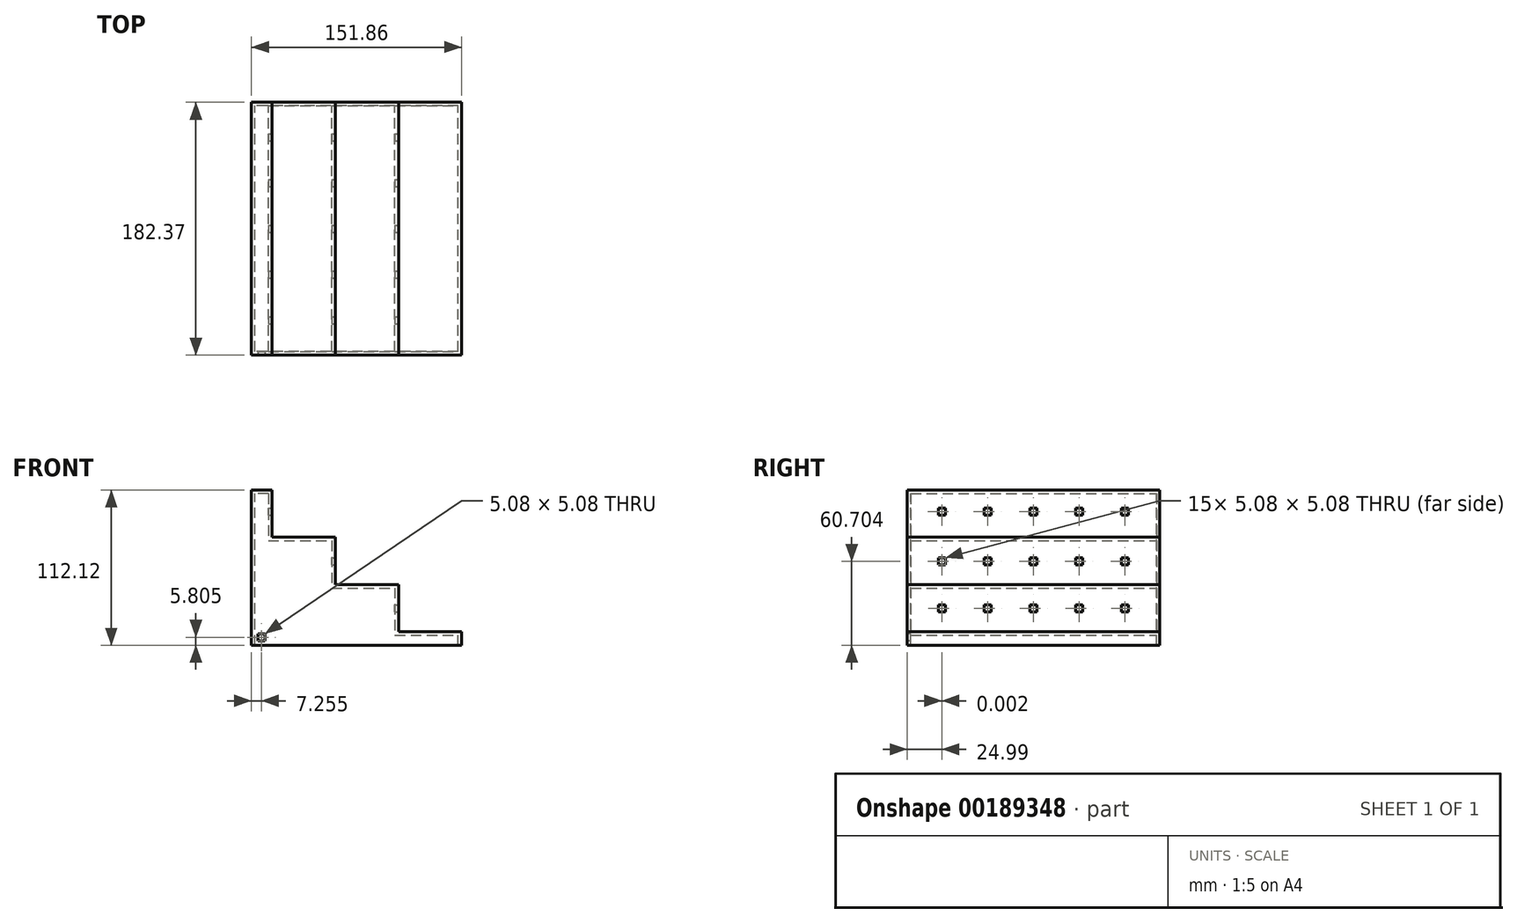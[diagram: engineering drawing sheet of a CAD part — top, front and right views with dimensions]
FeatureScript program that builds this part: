
annotation { "Feature Type Name" : "Feature", "Feature Type Description" : "" }
export const myFeature = defineFeature(function(context is Context, id is Id, definition is map)
    precondition{}
    {
        {
            var Q0;
            Q0=qCreatedBy(makeId("Front.planeOp"),FACE);
            var sketch = newSketch(context, id + "F0", { "sketchPlane" : qUnion([Q0])});
            skLineSegment(sketch, "E0.bottom", {"start": v(75.93, -56.06) * mm, "end": v(-75.93, -56.06) * mm});
            skLineSegment(sketch, "E0.top", {"start": v(75.93, 56.06) * mm, "end": v(-75.93, 56.06) * mm});
            skLineSegment(sketch, "E0.left", {"start": v(75.93, -56.06) * mm, "end": v(75.93, 56.06) * mm});
            skLineSegment(sketch, "E0.right", {"start": v(-75.93, -56.06) * mm, "end": v(-75.93, 56.06) * mm});
            skPoint(sketch, "E0.middle", {"position": v(0, 0) * mm});
            skLineSegment(sketch, "E1", {"start": v(-61.23, 56.06) * mm, "end": v(-61.23, -56.06) * mm});
            skLineSegment(sketch, "E2", {"start": v(-15.51, 56.06) * mm, "end": v(-15.51, -56.06) * mm});
            skLineSegment(sketch, "E3", {"start": v(30.2, 56.06) * mm, "end": v(30.2, -56.06) * mm});
            skLineSegment(sketch, "E4", {"start": v(-75.93, -46.26) * mm, "end": v(75.93, -46.26) * mm});
            skLineSegment(sketch, "E5", {"start": v(-75.93, 21.96) * mm, "end": v(75.93, 21.96) * mm});
            skLineSegment(sketch, "E6", {"start": v(-75.93, -12.15) * mm, "end": v(75.93, -12.15) * mm});
            skSolve(sketch);
        }
        {
            var Q0;
            {var subQ0=sQuery(id+"F0.wireOp",EDGE,"E0.right");var subQ1=sQuery(id+"F0.wireOp",EDGE,"E0.top");var subQ2=makeQuery(id+"F0.imprint","INTERSECT",VERTEX,{"derivedFrom":[subQ1,subQ0]});Q0=makeQuery(id+"F0.imprint","IMPRINT",FACE,{"disambiguationData":[TD([[makeQuery(id+"F0.imprint","IMPRINT",EDGE,{"disambiguationData":[TD([[subQ2,1.0]])],"derivedFrom":subQ1}),1.0]])]});}
            var Q1;
            {var subQ0=sQuery(id+"F0.wireOp",EDGE,"E5");var subQ1=sQuery(id+"F0.wireOp",EDGE,"E1");var subQ2=makeQuery(id+"F0.imprint","INTERSECT",VERTEX,{"derivedFrom":[subQ1,subQ0]});Q1=makeQuery(id+"F0.imprint","IMPRINT",FACE,{"disambiguationData":[TD([[makeQuery(id+"F0.imprint","IMPRINT",EDGE,{"disambiguationData":[TD([[subQ2,-1.0]])],"derivedFrom":subQ1}),1.0]])]});}
            var Q2;
            {var subQ0=sQuery(id+"F0.wireOp",EDGE,"E5");var subQ1=sQuery(id+"F0.wireOp",EDGE,"E0.right");var subQ2=makeQuery(id+"F0.imprint","INTERSECT",VERTEX,{"derivedFrom":[subQ1,subQ0]});Q2=makeQuery(id+"F0.imprint","IMPRINT",FACE,{"disambiguationData":[TD([[makeQuery(id+"F0.imprint","IMPRINT",EDGE,{"disambiguationData":[TD([[subQ2,1.0]])],"derivedFrom":subQ1}),-1.0]])]});}
            var Q3;
            {var subQ0=sQuery(id+"F0.wireOp",EDGE,"E4");var subQ1=sQuery(id+"F0.wireOp",EDGE,"E0.right");var subQ2=makeQuery(id+"F0.imprint","INTERSECT",VERTEX,{"derivedFrom":[subQ1,subQ0]});Q3=makeQuery(id+"F0.imprint","IMPRINT",FACE,{"disambiguationData":[TD([[makeQuery(id+"F0.imprint","IMPRINT",EDGE,{"disambiguationData":[TD([[subQ2,-1.0]])],"derivedFrom":subQ1}),-1.0]])]});}
            var Q4;
            {var subQ0=sQuery(id+"F0.wireOp",EDGE,"E0.right");var subQ1=sQuery(id+"F0.wireOp",EDGE,"E0.bottom");var subQ2=makeQuery(id+"F0.imprint","INTERSECT",VERTEX,{"derivedFrom":[subQ1,subQ0]});Q4=makeQuery(id+"F0.imprint","IMPRINT",FACE,{"disambiguationData":[TD([[makeQuery(id+"F0.imprint","IMPRINT",EDGE,{"disambiguationData":[TD([[subQ2,1.0]])],"derivedFrom":subQ1}),-1.0]])]});}
            var Q5;
            {var subQ0=sQuery(id+"F0.wireOp",EDGE,"E6");var subQ1=sQuery(id+"F0.wireOp",EDGE,"E1");var subQ2=makeQuery(id+"F0.imprint","INTERSECT",VERTEX,{"derivedFrom":[subQ1,subQ0]});Q5=makeQuery(id+"F0.imprint","IMPRINT",FACE,{"disambiguationData":[TD([[makeQuery(id+"F0.imprint","IMPRINT",EDGE,{"disambiguationData":[TD([[subQ2,-1.0]])],"derivedFrom":subQ1}),1.0]])]});}
            var Q6;
            {var subQ0=sQuery(id+"F0.wireOp",EDGE,"E1");var subQ1=sQuery(id+"F0.wireOp",EDGE,"E0.bottom");var subQ2=makeQuery(id+"F0.imprint","INTERSECT",VERTEX,{"derivedFrom":[subQ1,subQ0]});Q6=makeQuery(id+"F0.imprint","IMPRINT",FACE,{"disambiguationData":[TD([[makeQuery(id+"F0.imprint","IMPRINT",EDGE,{"disambiguationData":[TD([[subQ2,1.0]])],"derivedFrom":subQ1}),-1.0]])]});}
            var Q7;
            {var subQ0=sQuery(id+"F0.wireOp",EDGE,"E2");var subQ1=sQuery(id+"F0.wireOp",EDGE,"E0.bottom");var subQ2=makeQuery(id+"F0.imprint","INTERSECT",VERTEX,{"derivedFrom":[subQ1,subQ0]});Q7=makeQuery(id+"F0.imprint","IMPRINT",FACE,{"disambiguationData":[TD([[makeQuery(id+"F0.imprint","IMPRINT",EDGE,{"disambiguationData":[TD([[subQ2,1.0]])],"derivedFrom":subQ1}),-1.0]])]});}
            var Q8;
            {var subQ0=sQuery(id+"F0.wireOp",EDGE,"E0.left");var subQ1=sQuery(id+"F0.wireOp",EDGE,"E0.bottom");var subQ2=makeQuery(id+"F0.imprint","INTERSECT",VERTEX,{"derivedFrom":[subQ1,subQ0]});Q8=makeQuery(id+"F0.imprint","IMPRINT",FACE,{"disambiguationData":[TD([[makeQuery(id+"F0.imprint","IMPRINT",EDGE,{"disambiguationData":[TD([[subQ2,-1.0]])],"derivedFrom":subQ1}),-1.0]])]});}
            var Q9;
            {var subQ0=sQuery(id+"F0.wireOp",EDGE,"E6");var subQ1=sQuery(id+"F0.wireOp",EDGE,"E2");var subQ2=makeQuery(id+"F0.imprint","INTERSECT",VERTEX,{"derivedFrom":[subQ1,subQ0]});Q9=makeQuery(id+"F0.imprint","IMPRINT",FACE,{"disambiguationData":[TD([[makeQuery(id+"F0.imprint","IMPRINT",EDGE,{"disambiguationData":[TD([[subQ2,-1.0]])],"derivedFrom":subQ1}),1.0]])]});}
            extrude(context, id + "F1", {"entities" : qUnion([Q0, Q1, Q2, Q3, Q4, Q5, Q6, Q7, Q8, Q9]), "depth" : 182.37 * mm});
        }
        {
            var Q0;
            Q0=makeQuery(id+"F1.opExtrude","SWEPT_FACE",FACE,{"disambiguationData":[OSD([sQuery(id+"F0.wireOp",EDGE,"E0.bottom")])]});
            shell(context, id + "F2", {"entities" : qUnion([Q0]), "thickness" : 2.54 * mm});
        }
        {
            var Q0;
            Q0=makeQuery(id+"F1.opExtrude","SWEPT_FACE",FACE,{"disambiguationData":[OSD([sQuery(id+"F0.wireOp",EDGE,"E3")])]});
            var sketch = newSketch(context, id + "F3", { "sketchPlane" : qUnion([Q0])});
            skLineSegment(sketch, "E7", {"start": v(-182.37, -29.2) * mm, "end": v(0, -29.2) * mm});
            skLineSegment(sketch, "E8.bottom", {"start": v(-154.69, -31.75) * mm, "end": v(-159.77, -31.75) * mm});
            skLineSegment(sketch, "E8.top", {"start": v(-154.69, -26.67) * mm, "end": v(-159.77, -26.67) * mm});
            skLineSegment(sketch, "E8.left", {"start": v(-154.69, -31.75) * mm, "end": v(-154.69, -26.67) * mm});
            skLineSegment(sketch, "E8.right", {"start": v(-159.77, -31.75) * mm, "end": v(-159.77, -26.67) * mm});
            skPoint(sketch, "E8.middle", {"position": v(-157.23, -29.2) * mm});
            skLineSegment(sketch, "E9.bottom", {"start": v(-121.67, -31.75) * mm, "end": v(-126.75, -31.75) * mm});
            skLineSegment(sketch, "E9.top", {"start": v(-121.67, -26.67) * mm, "end": v(-126.75, -26.67) * mm});
            skLineSegment(sketch, "E9.left", {"start": v(-121.67, -31.75) * mm, "end": v(-121.67, -26.67) * mm});
            skLineSegment(sketch, "E9.right", {"start": v(-126.75, -31.75) * mm, "end": v(-126.75, -26.67) * mm});
            skPoint(sketch, "E9.middle", {"position": v(-124.2, -29.2) * mm});
            skLineSegment(sketch, "E10.bottom", {"start": v(-88.65, -31.75) * mm, "end": v(-93.73, -31.75) * mm});
            skLineSegment(sketch, "E10.top", {"start": v(-88.65, -26.67) * mm, "end": v(-93.73, -26.67) * mm});
            skLineSegment(sketch, "E10.left", {"start": v(-88.65, -31.75) * mm, "end": v(-88.65, -26.67) * mm});
            skLineSegment(sketch, "E10.right", {"start": v(-93.73, -31.75) * mm, "end": v(-93.73, -26.67) * mm});
            skPoint(sketch, "E10.middle", {"position": v(-91.19, -29.2) * mm});
            skLineSegment(sketch, "E11.bottom", {"start": v(-55.63, -31.75) * mm, "end": v(-60.7, -31.75) * mm});
            skLineSegment(sketch, "E11.top", {"start": v(-55.63, -26.67) * mm, "end": v(-60.7, -26.67) * mm});
            skLineSegment(sketch, "E11.left", {"start": v(-55.63, -31.75) * mm, "end": v(-55.63, -26.67) * mm});
            skLineSegment(sketch, "E11.right", {"start": v(-60.7, -31.75) * mm, "end": v(-60.7, -26.67) * mm});
            skPoint(sketch, "E11.middle", {"position": v(-58.17, -29.2) * mm});
            skLineSegment(sketch, "E12.bottom", {"start": v(-22.6, -31.75) * mm, "end": v(-27.69, -31.75) * mm});
            skLineSegment(sketch, "E12.top", {"start": v(-22.6, -26.67) * mm, "end": v(-27.69, -26.67) * mm});
            skLineSegment(sketch, "E12.left", {"start": v(-22.6, -31.75) * mm, "end": v(-22.6, -26.67) * mm});
            skLineSegment(sketch, "E12.right", {"start": v(-27.69, -31.75) * mm, "end": v(-27.69, -26.67) * mm});
            skPoint(sketch, "E12.middle", {"position": v(-25.15, -29.2) * mm});
            skSolve(sketch);
        }
        {
            var Q0;
            {var subQ5=sQuery(id+"F3.wireOp",EDGE,"E8.top");Q0=makeQuery(id+"F3.imprint","IMPRINT",FACE,{"disambiguationData":[TD([[makeQuery(id+"F3.imprint","IMPRINT",EDGE,{"derivedFrom":subQ5}),1.0]])]});}
            var Q1;
            {var subQ5=sQuery(id+"F3.wireOp",EDGE,"E8.bottom");Q1=makeQuery(id+"F3.imprint","IMPRINT",FACE,{"disambiguationData":[TD([[makeQuery(id+"F3.imprint","IMPRINT",EDGE,{"derivedFrom":subQ5}),-1.0]])]});}
            var Q2;
            {var subQ5=sQuery(id+"F3.wireOp",EDGE,"E9.bottom");Q2=makeQuery(id+"F3.imprint","IMPRINT",FACE,{"disambiguationData":[TD([[makeQuery(id+"F3.imprint","IMPRINT",EDGE,{"derivedFrom":subQ5}),-1.0]])]});}
            var Q3;
            {var subQ5=sQuery(id+"F3.wireOp",EDGE,"E9.top");Q3=makeQuery(id+"F3.imprint","IMPRINT",FACE,{"disambiguationData":[TD([[makeQuery(id+"F3.imprint","IMPRINT",EDGE,{"derivedFrom":subQ5}),1.0]])]});}
            var Q4;
            {var subQ5=sQuery(id+"F3.wireOp",EDGE,"E10.bottom");Q4=makeQuery(id+"F3.imprint","IMPRINT",FACE,{"disambiguationData":[TD([[makeQuery(id+"F3.imprint","IMPRINT",EDGE,{"derivedFrom":subQ5}),-1.0]])]});}
            var Q5;
            {var subQ5=sQuery(id+"F3.wireOp",EDGE,"E10.top");Q5=makeQuery(id+"F3.imprint","IMPRINT",FACE,{"disambiguationData":[TD([[makeQuery(id+"F3.imprint","IMPRINT",EDGE,{"derivedFrom":subQ5}),1.0]])]});}
            var Q6;
            {var subQ5=sQuery(id+"F3.wireOp",EDGE,"E11.bottom");Q6=makeQuery(id+"F3.imprint","IMPRINT",FACE,{"disambiguationData":[TD([[makeQuery(id+"F3.imprint","IMPRINT",EDGE,{"derivedFrom":subQ5}),-1.0]])]});}
            var Q7;
            {var subQ5=sQuery(id+"F3.wireOp",EDGE,"E11.top");Q7=makeQuery(id+"F3.imprint","IMPRINT",FACE,{"disambiguationData":[TD([[makeQuery(id+"F3.imprint","IMPRINT",EDGE,{"derivedFrom":subQ5}),1.0]])]});}
            var Q8;
            {var subQ5=sQuery(id+"F3.wireOp",EDGE,"E12.top");Q8=makeQuery(id+"F3.imprint","IMPRINT",FACE,{"disambiguationData":[TD([[makeQuery(id+"F3.imprint","IMPRINT",EDGE,{"derivedFrom":subQ5}),1.0]])]});}
            var Q9;
            {var subQ5=sQuery(id+"F3.wireOp",EDGE,"E12.bottom");Q9=makeQuery(id+"F3.imprint","IMPRINT",FACE,{"disambiguationData":[TD([[makeQuery(id+"F3.imprint","IMPRINT",EDGE,{"derivedFrom":subQ5}),-1.0]])]});}
            extrude(context, id + "F4", {"entities" : qUnion([Q0, Q1, Q2, Q3, Q4, Q5, Q6, Q7, Q8, Q9]), "operationType" : NewBodyOperationType.REMOVE, "oppositeDirection" : true, "depth" : 25.4 * mm});
        }
        {
            var Q0;
            Q0=makeQuery(id+"F1.opExtrude","CAP_FACE",FACE,{"disambiguationData":[OSD([sQuery(id+"F0.wireOp",EDGE,"E0.bottom"),sQuery(id+"F0.wireOp",EDGE,"E0.top"),sQuery(id+"F0.wireOp",EDGE,"E0.left"),sQuery(id+"F0.wireOp",EDGE,"E0.right"),sQuery(id+"F0.wireOp",EDGE,"E1"),sQuery(id+"F0.wireOp",EDGE,"E2"),sQuery(id+"F0.wireOp",EDGE,"E3"),sQuery(id+"F0.wireOp",EDGE,"E4"),sQuery(id+"F0.wireOp",EDGE,"E5"),sQuery(id+"F0.wireOp",EDGE,"E6")])],"isStart":false});
            var sketch = newSketch(context, id + "F5", { "sketchPlane" : qUnion([Q0])});
            skLineSegment(sketch, "E13.bottom", {"start": v(-71.22, -52.8) * mm, "end": v(-66.14, -52.8) * mm});
            skLineSegment(sketch, "E13.top", {"start": v(-71.22, -47.72) * mm, "end": v(-66.14, -47.72) * mm});
            skLineSegment(sketch, "E13.left", {"start": v(-71.22, -52.8) * mm, "end": v(-71.22, -47.72) * mm});
            skLineSegment(sketch, "E13.right", {"start": v(-66.14, -52.8) * mm, "end": v(-66.14, -47.72) * mm});
            skPoint(sketch, "E13.middle", {"position": v(-68.68, -50.26) * mm});
            skSolve(sketch);
        }
        {
            var Q0;
            Q0=makeQuery(id+"F5.imprint","IMPRINT",FACE,{"disambiguationData":[TD([[makeQuery(id+"F5.imprint","IMPRINT",EDGE,{"derivedFrom":sQuery(id+"F5.wireOp",EDGE,"E13.bottom")}),1.0]])]});
            extrude(context, id + "F6", {"entities" : qUnion([Q0]), "operationType" : NewBodyOperationType.REMOVE, "oppositeDirection" : true, "depth" : 25.4 * mm});
        }
        {
            var Q0;
            Q0=makeQuery(id+"F1.opExtrude","SWEPT_FACE",FACE,{"disambiguationData":[OSD([sQuery(id+"F0.wireOp",EDGE,"E2")])]});
            var sketch = newSketch(context, id + "F7", { "sketchPlane" : qUnion([Q0])});
            skLineSegment(sketch, "E14", {"start": v(-182.53, 4.64) * mm, "end": v(-0.15, 4.64) * mm});
            skLineSegment(sketch, "E15.bottom", {"start": v(-154.84, 2.1) * mm, "end": v(-159.92, 2.1) * mm});
            skLineSegment(sketch, "E15.top", {"start": v(-154.84, 7.18) * mm, "end": v(-159.92, 7.18) * mm});
            skLineSegment(sketch, "E15.left", {"start": v(-154.84, 2.1) * mm, "end": v(-154.84, 7.18) * mm});
            skLineSegment(sketch, "E15.right", {"start": v(-159.92, 2.1) * mm, "end": v(-159.92, 7.18) * mm});
            skPoint(sketch, "E15.middle", {"position": v(-157.38, 4.64) * mm});
            skLineSegment(sketch, "E16.bottom", {"start": v(-121.82, 2.1) * mm, "end": v(-126.9, 2.1) * mm});
            skLineSegment(sketch, "E16.top", {"start": v(-121.82, 7.18) * mm, "end": v(-126.9, 7.18) * mm});
            skLineSegment(sketch, "E16.left", {"start": v(-121.82, 2.1) * mm, "end": v(-121.82, 7.18) * mm});
            skLineSegment(sketch, "E16.right", {"start": v(-126.9, 2.1) * mm, "end": v(-126.9, 7.18) * mm});
            skPoint(sketch, "E16.middle", {"position": v(-124.36, 4.64) * mm});
            skLineSegment(sketch, "E17.bottom", {"start": v(-88.8, 2.1) * mm, "end": v(-93.88, 2.1) * mm});
            skLineSegment(sketch, "E17.top", {"start": v(-88.8, 7.18) * mm, "end": v(-93.88, 7.18) * mm});
            skLineSegment(sketch, "E17.left", {"start": v(-88.8, 2.1) * mm, "end": v(-88.8, 7.18) * mm});
            skLineSegment(sketch, "E17.right", {"start": v(-93.88, 2.1) * mm, "end": v(-93.88, 7.18) * mm});
            skPoint(sketch, "E17.middle", {"position": v(-91.34, 4.64) * mm});
            skLineSegment(sketch, "E18.bottom", {"start": v(-55.78, 2.1) * mm, "end": v(-60.86, 2.1) * mm});
            skLineSegment(sketch, "E18.top", {"start": v(-55.78, 7.18) * mm, "end": v(-60.86, 7.18) * mm});
            skLineSegment(sketch, "E18.left", {"start": v(-55.78, 2.1) * mm, "end": v(-55.78, 7.18) * mm});
            skLineSegment(sketch, "E18.right", {"start": v(-60.86, 2.1) * mm, "end": v(-60.86, 7.18) * mm});
            skPoint(sketch, "E18.middle", {"position": v(-58.32, 4.64) * mm});
            skLineSegment(sketch, "E19.bottom", {"start": v(-22.76, 2.1) * mm, "end": v(-27.84, 2.1) * mm});
            skLineSegment(sketch, "E19.top", {"start": v(-22.76, 7.18) * mm, "end": v(-27.84, 7.18) * mm});
            skLineSegment(sketch, "E19.left", {"start": v(-22.76, 2.1) * mm, "end": v(-22.76, 7.18) * mm});
            skLineSegment(sketch, "E19.right", {"start": v(-27.84, 2.1) * mm, "end": v(-27.84, 7.18) * mm});
            skPoint(sketch, "E19.middle", {"position": v(-25.3, 4.64) * mm});
            skSolve(sketch);
        }
        {
            var Q0;
            {var subQ5=sQuery(id+"F7.wireOp",EDGE,"E15.top");Q0=makeQuery(id+"F7.imprint","IMPRINT",FACE,{"disambiguationData":[TD([[makeQuery(id+"F7.imprint","IMPRINT",EDGE,{"derivedFrom":subQ5}),1.0]])]});}
            var Q1;
            {var subQ5=sQuery(id+"F7.wireOp",EDGE,"E15.bottom");Q1=makeQuery(id+"F7.imprint","IMPRINT",FACE,{"disambiguationData":[TD([[makeQuery(id+"F7.imprint","IMPRINT",EDGE,{"derivedFrom":subQ5}),-1.0]])]});}
            var Q2;
            {var subQ5=sQuery(id+"F7.wireOp",EDGE,"E16.top");Q2=makeQuery(id+"F7.imprint","IMPRINT",FACE,{"disambiguationData":[TD([[makeQuery(id+"F7.imprint","IMPRINT",EDGE,{"derivedFrom":subQ5}),1.0]])]});}
            var Q3;
            {var subQ5=sQuery(id+"F7.wireOp",EDGE,"E16.bottom");Q3=makeQuery(id+"F7.imprint","IMPRINT",FACE,{"disambiguationData":[TD([[makeQuery(id+"F7.imprint","IMPRINT",EDGE,{"derivedFrom":subQ5}),-1.0]])]});}
            var Q4;
            {var subQ5=sQuery(id+"F7.wireOp",EDGE,"E17.top");Q4=makeQuery(id+"F7.imprint","IMPRINT",FACE,{"disambiguationData":[TD([[makeQuery(id+"F7.imprint","IMPRINT",EDGE,{"derivedFrom":subQ5}),1.0]])]});}
            var Q5;
            {var subQ5=sQuery(id+"F7.wireOp",EDGE,"E17.bottom");Q5=makeQuery(id+"F7.imprint","IMPRINT",FACE,{"disambiguationData":[TD([[makeQuery(id+"F7.imprint","IMPRINT",EDGE,{"derivedFrom":subQ5}),-1.0]])]});}
            var Q6;
            {var subQ5=sQuery(id+"F7.wireOp",EDGE,"E18.top");Q6=makeQuery(id+"F7.imprint","IMPRINT",FACE,{"disambiguationData":[TD([[makeQuery(id+"F7.imprint","IMPRINT",EDGE,{"derivedFrom":subQ5}),1.0]])]});}
            var Q7;
            {var subQ5=sQuery(id+"F7.wireOp",EDGE,"E18.bottom");Q7=makeQuery(id+"F7.imprint","IMPRINT",FACE,{"disambiguationData":[TD([[makeQuery(id+"F7.imprint","IMPRINT",EDGE,{"derivedFrom":subQ5}),-1.0]])]});}
            var Q8;
            {var subQ5=sQuery(id+"F7.wireOp",EDGE,"E19.top");Q8=makeQuery(id+"F7.imprint","IMPRINT",FACE,{"disambiguationData":[TD([[makeQuery(id+"F7.imprint","IMPRINT",EDGE,{"derivedFrom":subQ5}),1.0]])]});}
            var Q9;
            {var subQ5=sQuery(id+"F7.wireOp",EDGE,"E19.bottom");Q9=makeQuery(id+"F7.imprint","IMPRINT",FACE,{"disambiguationData":[TD([[makeQuery(id+"F7.imprint","IMPRINT",EDGE,{"derivedFrom":subQ5}),-1.0]])]});}
            extrude(context, id + "F8", {"entities" : qUnion([Q0, Q1, Q2, Q3, Q4, Q5, Q6, Q7, Q8, Q9]), "operationType" : NewBodyOperationType.REMOVE, "oppositeDirection" : true, "depth" : 25.4 * mm});
        }
        {
            var Q0;
            Q0=makeQuery(id+"F1.opExtrude","SWEPT_FACE",FACE,{"disambiguationData":[OSD([sQuery(id+"F0.wireOp",EDGE,"E1")])]});
            var sketch = newSketch(context, id + "F9", { "sketchPlane" : qUnion([Q0])});
            skLineSegment(sketch, "E20", {"start": v(-182.52, 40.47) * mm, "end": v(-0.15, 40.47) * mm});
            skLineSegment(sketch, "E21.bottom", {"start": v(-154.84, 37.93) * mm, "end": v(-159.92, 37.93) * mm});
            skLineSegment(sketch, "E21.top", {"start": v(-154.84, 43) * mm, "end": v(-159.92, 43) * mm});
            skLineSegment(sketch, "E21.left", {"start": v(-154.84, 37.93) * mm, "end": v(-154.84, 43) * mm});
            skLineSegment(sketch, "E21.right", {"start": v(-159.92, 37.93) * mm, "end": v(-159.92, 43) * mm});
            skPoint(sketch, "E21.middle", {"position": v(-157.38, 40.47) * mm});
            skLineSegment(sketch, "E22.bottom", {"start": v(-121.82, 37.93) * mm, "end": v(-126.9, 37.93) * mm});
            skLineSegment(sketch, "E22.top", {"start": v(-121.82, 43) * mm, "end": v(-126.9, 43) * mm});
            skLineSegment(sketch, "E22.left", {"start": v(-121.82, 37.93) * mm, "end": v(-121.82, 43) * mm});
            skLineSegment(sketch, "E22.right", {"start": v(-126.9, 37.93) * mm, "end": v(-126.9, 43) * mm});
            skPoint(sketch, "E22.middle", {"position": v(-124.36, 40.47) * mm});
            skLineSegment(sketch, "E23.bottom", {"start": v(-88.8, 37.93) * mm, "end": v(-93.88, 37.93) * mm});
            skLineSegment(sketch, "E23.top", {"start": v(-88.8, 43) * mm, "end": v(-93.88, 43) * mm});
            skLineSegment(sketch, "E23.left", {"start": v(-88.8, 37.93) * mm, "end": v(-88.8, 43) * mm});
            skLineSegment(sketch, "E23.right", {"start": v(-93.88, 37.93) * mm, "end": v(-93.88, 43) * mm});
            skPoint(sketch, "E23.middle", {"position": v(-91.34, 40.47) * mm});
            skLineSegment(sketch, "E24.bottom", {"start": v(-55.78, 37.93) * mm, "end": v(-60.86, 37.93) * mm});
            skLineSegment(sketch, "E24.top", {"start": v(-55.78, 43) * mm, "end": v(-60.86, 43) * mm});
            skLineSegment(sketch, "E24.left", {"start": v(-55.78, 37.93) * mm, "end": v(-55.78, 43) * mm});
            skLineSegment(sketch, "E24.right", {"start": v(-60.86, 37.93) * mm, "end": v(-60.86, 43) * mm});
            skPoint(sketch, "E24.middle", {"position": v(-58.32, 40.47) * mm});
            skLineSegment(sketch, "E25.bottom", {"start": v(-22.76, 37.93) * mm, "end": v(-27.84, 37.93) * mm});
            skLineSegment(sketch, "E25.top", {"start": v(-22.76, 43) * mm, "end": v(-27.84, 43) * mm});
            skLineSegment(sketch, "E25.left", {"start": v(-22.76, 37.93) * mm, "end": v(-22.76, 43) * mm});
            skLineSegment(sketch, "E25.right", {"start": v(-27.84, 37.93) * mm, "end": v(-27.84, 43) * mm});
            skPoint(sketch, "E25.middle", {"position": v(-25.3, 40.47) * mm});
            skSolve(sketch);
        }
        {
            var Q0;
            {var subQ5=sQuery(id+"F9.wireOp",EDGE,"E21.top");Q0=makeQuery(id+"F9.imprint","IMPRINT",FACE,{"disambiguationData":[TD([[makeQuery(id+"F9.imprint","IMPRINT",EDGE,{"derivedFrom":subQ5}),1.0]])]});}
            var Q1;
            {var subQ5=sQuery(id+"F9.wireOp",EDGE,"E21.bottom");Q1=makeQuery(id+"F9.imprint","IMPRINT",FACE,{"disambiguationData":[TD([[makeQuery(id+"F9.imprint","IMPRINT",EDGE,{"derivedFrom":subQ5}),-1.0]])]});}
            var Q2;
            {var subQ5=sQuery(id+"F9.wireOp",EDGE,"E22.top");Q2=makeQuery(id+"F9.imprint","IMPRINT",FACE,{"disambiguationData":[TD([[makeQuery(id+"F9.imprint","IMPRINT",EDGE,{"derivedFrom":subQ5}),1.0]])]});}
            var Q3;
            {var subQ5=sQuery(id+"F9.wireOp",EDGE,"E22.bottom");Q3=makeQuery(id+"F9.imprint","IMPRINT",FACE,{"disambiguationData":[TD([[makeQuery(id+"F9.imprint","IMPRINT",EDGE,{"derivedFrom":subQ5}),-1.0]])]});}
            var Q4;
            {var subQ5=sQuery(id+"F9.wireOp",EDGE,"E23.top");Q4=makeQuery(id+"F9.imprint","IMPRINT",FACE,{"disambiguationData":[TD([[makeQuery(id+"F9.imprint","IMPRINT",EDGE,{"derivedFrom":subQ5}),1.0]])]});}
            var Q5;
            {var subQ5=sQuery(id+"F9.wireOp",EDGE,"E23.bottom");Q5=makeQuery(id+"F9.imprint","IMPRINT",FACE,{"disambiguationData":[TD([[makeQuery(id+"F9.imprint","IMPRINT",EDGE,{"derivedFrom":subQ5}),-1.0]])]});}
            var Q6;
            {var subQ5=sQuery(id+"F9.wireOp",EDGE,"E24.top");Q6=makeQuery(id+"F9.imprint","IMPRINT",FACE,{"disambiguationData":[TD([[makeQuery(id+"F9.imprint","IMPRINT",EDGE,{"derivedFrom":subQ5}),1.0]])]});}
            var Q7;
            {var subQ5=sQuery(id+"F9.wireOp",EDGE,"E24.bottom");Q7=makeQuery(id+"F9.imprint","IMPRINT",FACE,{"disambiguationData":[TD([[makeQuery(id+"F9.imprint","IMPRINT",EDGE,{"derivedFrom":subQ5}),-1.0]])]});}
            var Q8;
            {var subQ5=sQuery(id+"F9.wireOp",EDGE,"E25.top");Q8=makeQuery(id+"F9.imprint","IMPRINT",FACE,{"disambiguationData":[TD([[makeQuery(id+"F9.imprint","IMPRINT",EDGE,{"derivedFrom":subQ5}),1.0]])]});}
            var Q9;
            {var subQ5=sQuery(id+"F9.wireOp",EDGE,"E25.bottom");Q9=makeQuery(id+"F9.imprint","IMPRINT",FACE,{"disambiguationData":[TD([[makeQuery(id+"F9.imprint","IMPRINT",EDGE,{"derivedFrom":subQ5}),-1.0]])]});}
            extrude(context, id + "F10", {"entities" : qUnion([Q0, Q1, Q2, Q3, Q4, Q5, Q6, Q7, Q8, Q9]), "operationType" : NewBodyOperationType.REMOVE, "oppositeDirection" : true, "depth" : 10.36 * mm});
        }
    });
